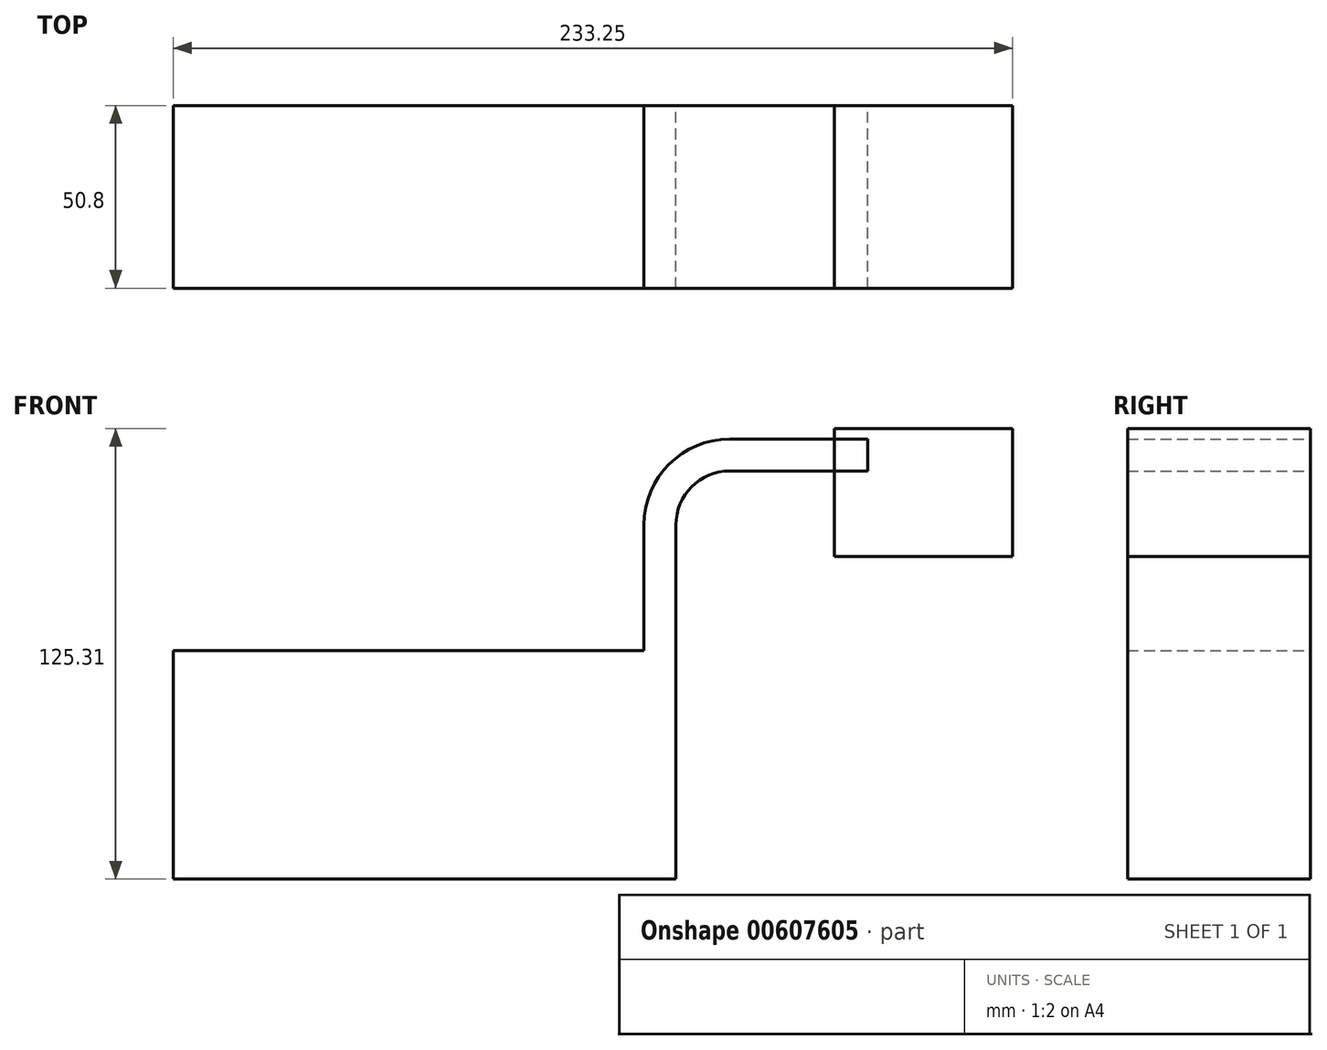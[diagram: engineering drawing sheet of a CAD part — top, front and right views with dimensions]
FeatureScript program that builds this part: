
annotation { "Feature Type Name" : "Feature", "Feature Type Description" : "" }
export const myFeature = defineFeature(function(context is Context, id is Id, definition is map)
    precondition{}
    {
        {
            var Q0;
            Q0=qCreatedBy(makeId("Front.planeOp"),FACE);
            var sketch = newSketch(context, id + "F0", { "sketchPlane" : qUnion([Q0])});
            skLineSegment(sketch, "E0.bottom", {"start": v(-69.85, -31.75) * mm, "end": v(69.85, -31.75) * mm});
            skLineSegment(sketch, "E0.top", {"start": v(-69.85, 31.75) * mm, "end": v(69.85, 31.75) * mm});
            skLineSegment(sketch, "E0.left", {"start": v(-69.85, -31.75) * mm, "end": v(-69.85, 31.75) * mm});
            skLineSegment(sketch, "E0.right", {"start": v(69.85, -31.75) * mm, "end": v(69.85, 31.75) * mm});
            skPoint(sketch, "E0.middle", {"position": v(0, 0) * mm});
            skLineSegment(sketch, "E1.bottom", {"start": v(163.4, 58) * mm, "end": v(113.87, 58) * mm});
            skLineSegment(sketch, "E1.top", {"start": v(163.4, 93.56) * mm, "end": v(113.87, 93.56) * mm});
            skLineSegment(sketch, "E1.left", {"start": v(163.4, 58) * mm, "end": v(163.4, 93.56) * mm});
            skLineSegment(sketch, "E1.right", {"start": v(113.87, 58) * mm, "end": v(113.87, 93.56) * mm});
            skPoint(sketch, "E1.middle", {"position": v(138.64, 75.78) * mm});
            skLineSegment(sketch, "E2", {"start": v(69.85, 31.75) * mm, "end": v(69.85, 66.75) * mm});
            skArc(sketch, "E3", {"start": v(69.85, 66.75) * mm, "mid": v(74.24, 77.35) * mm, "end": v(84.84, 81.74) * mm});
            skLineSegment(sketch, "E4", {"start": v(84.84, 81.74) * mm, "end": v(123.18, 81.74) * mm});
            skLineSegment(sketch, "E5.0", {"start": v(84.84, 90.63) * mm, "end": v(123.18, 90.63) * mm});
            skArc(sketch, "E5.1", {"start": v(60.96, 66.75) * mm, "mid": v(67.95, 83.64) * mm, "end": v(84.84, 90.63) * mm});
            skLineSegment(sketch, "E5.2", {"start": v(60.96, 31.75) * mm, "end": v(60.96, 66.75) * mm});
            skLineSegment(sketch, "E6", {"start": v(123.18, 81.74) * mm, "end": v(123.18, 90.63) * mm});
            skSolve(sketch);
        }
        {
            var Q0;
            Q0=makeQuery(id+"F0.imprint","IMPRINT",FACE,{"disambiguationData":[TD([[makeQuery(id+"F0.imprint","IMPRINT",EDGE,{"derivedFrom":sQuery(id+"F0.wireOp",EDGE,"E0.bottom")}),1.0]])]});
            var Q1;
            {var subQ0=sQuery(id+"F0.wireOp",EDGE,"E2");Q1=makeQuery(id+"F0.imprint","IMPRINT",FACE,{"disambiguationData":[TD([[makeQuery(id+"F0.imprint","IMPRINT",EDGE,{"derivedFrom":subQ0}),1.0]])]});}
            var Q2;
            {var subQ1=sQuery(id+"F0.wireOp",EDGE,"E1.bottom");Q2=makeQuery(id+"F0.imprint","IMPRINT",FACE,{"disambiguationData":[TD([[makeQuery(id+"F0.imprint","IMPRINT",EDGE,{"derivedFrom":subQ1}),-1.0]])]});}
            extrude(context, id + "F1", {"entities" : qUnion([Q0, Q1, Q2]), "endBound" : BoundingType.SYMMETRIC, "depth" : 50.8 * mm, "offsetDistance" : 25.4 * mm});
        }
    });
